# Revit family: IS_Tesi_T0079_BIM_ES
name_source: partatom
category: Plumbing Fixtures
units: mm (PartAtom-declared; Revit-internal decimal feet)

## family parameters
Cut with Voids When Loaded = No
Host = Face
OmniClass Number = 23.45.05.21.11.11
OmniClass Title = Water Operated Water Closets
Part Type = Normal
Room Calculation Point = No
Round Connector Dimension = Use Diameter
Shared = No

## types (2) — shared parameters
Accesorios = https://www.idealstandard.es
Assembly Code = C1030200
Autor = Ideal Standard s.l.u. (ESP)
Ayuda = https://www.idealstandard.es
ColorWc = Blanco
CódigoDeBarras = 8014140435235
Default Elevation = 400 mm  [stored 1.31234 ft]
DescripciónUniclass2015 = WCPANS
Description = Inodoro suspendido TESI con fijación oculta y Aquablade, blanco
Destacado = Inodoro suspendido con fijación oculta y Aquablade, blanco
Espacio = Interno
FechaDeCreación = 2017-01-28
Forma = Escultural
GarantíaDeLasPiezas = 2
GarantíaPiezas = 2
GuíaDeInstallación = https://www.idealstandard.es
IfcExportaComo = WCPANS
InformaciónDeProducto = https://www.idealstandard.es
Manufacturer = https://www.idealstandard.es
Marca = Ideal Standard Iberia
Material = Porcelana vitrificada
MaterialWc = Porcelana vitrificada
Nombre = WcPans_Tesi_T007901_IdealStandard
NombreDeObjetoBim = IS_IdealStandard_WcPans_Tesi_T0079
NominalHeight = 337 mm
NominalLength = 530 mm
NominalWidth = 360 mm
PesoNeto = 22.00 Kg
ReferenciaDeModelo = Inodoro suspendido con fijación oculta y Aquablade, blanco
ReferenciaUniclass2015 = Pr_40_20_93_94
Repuestos = https://www.idealstandard.es
Size = 530 x 361 x 337 mm
Teléfono = +34 93 561 80 00
TipoDeConexión = Fontaneria
TipoDeExportaciónIfc = TOILETPAN
TipoDeGarantía = Garantía del Fabricante
TipoDeTaza = Suspendido
TipoMontajeWc = Suspendido
TipoWc = 0
URL = https://www.idealstandard.es
UnidadDeVolúmen = Litros
UnidadDeÁrea = milímetros
UnidadGarantía = año
UnidadLineal = milímetros
Versión = 1
zero-valued in all types: CWFU, Cost, HWFU, NivelDeDesbordamiento, NominalDepth, PesoBruto, WFU

## per-type parameters (varying)
| type | Acabado | Color | Finish | Model | NúmeroDeModelo | Referencia |
| T007901 - Inodoro suspendido TESI con fijación oculta y Aquablade, blanco | Blanco | Blanco | IS_RenderMaterial_VitreousChina_Silk_White | T007901 | T007901 | T007901 |
| T0079V3 - Inodoro suspendido TESI con fijación oculta y Aquablade, Negro Seda | Negro Seda | Negro Seda | IS_RenderMaterial_VitreousChina_Silk_Black | T0079V3 | T0079V3 | T0079V3 |

note: [stored X ft] marks values corroborated as IEEE doubles in the binary element streams (Revit-internal decimal feet)

## geometry (parser evidence)
native form markers: Sweep x3
no freeform markers — native parametric forms only
